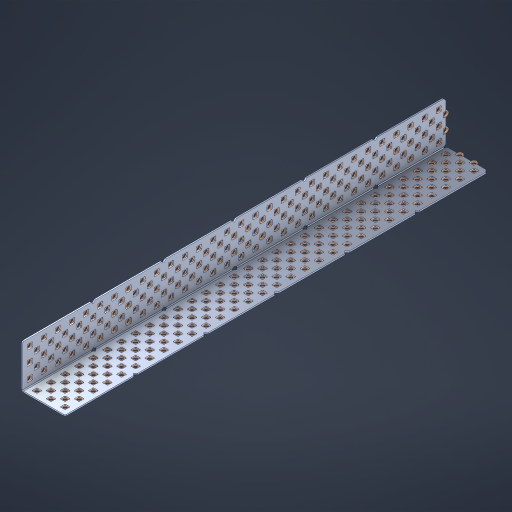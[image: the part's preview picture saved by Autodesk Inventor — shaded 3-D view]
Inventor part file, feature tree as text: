
AUTODESK INVENTOR PART (.ipt)
format: ipt  version: 2023 (Build 270158000, 158)  size: 3,007,488 bytes
history: native  units: in
note: dims shown in document units (in); Inventor stores cm internally (conversion verified against a paired STEP export)
features: other x306, extrude x298, sheet_metal_op x8, sketch x7, pattern_linear x3, mirror x1, chamfer x1
ambient origin geometry x8: Origin, YZ Plane, XZ Plane, XY Plane, X Axis, Y Axis, Z Axis, Center Point
bodies: Solid1 (feature_tree), Body (feature_tree)
feature tree (624):
  sheet_metal_op  "Flanges"
  sheet_metal_op  "Body Pattern"
  pattern_linear  "Center Double"  Spacing1=1.5in  [1 undecoded]
  pattern_linear  "Center Pattern"  Spacing1=0.1875in  [1 undecoded]
  other  "Arc Length"
  pattern_linear  "Notch Pattern"  Spacing1=0.0469in  [1 undecoded]
  other  "Diagonal Plane"
  mirror  "Everything Mirrored"
  chamfer  "End Chamfer"
  sketch  "Sketch1"  dims[d0=1.5in]
  other  "Plate1"
  sketch  "Sketch2"  dims[d1=15.0in]
  other  "Plate2"
  sheet_metal_op  "Bend1"
  sheet_metal_op  "Corner1"
  sketch  "Sketch8"  dims[d2=0.0469in]
  sketch  "Sketch9"  dims[d3=0.0469in]
  other  "Srf91"
  sheet_metal_op  "Body Pattern Sketch"
  other  "Srf92"
  sketch  "Sketch13"  dims[d4=0.0234in]
  sketch  "Sketch15"  dims[d5=0.0938in]
  sketch  "Sketch16"  dims[d6=0.0469in d7=1.5in d8=90.0deg d9=0.0312in d10=0.1875in d11=0.0469in d12=0.0469in d49=0.182in d50=0.02in d52=0.25in d53=0.0469in d54=0.0in d55=0.172in d56=1.0in d57=0.0in d85=0.1473in d86=0.1659in d89=0.0469in d90=0.0in d91=0.04in d92=0.0491in d95=2.5in d96=0.04in d97=0.25in d98=45.0deg d106=0.182in d107=0.02in d110=0.0469in d111=0.0in d112=0.172in d113=0.5in d114=0.0in d117=0.5in d126=0.0491in d127=0.1227in d128=0.08in d129=0.04in d130=2.5in d131=0.25in d132=11.811in d134=0.5in d135=1.1811in d137=0.5in d140=0.5in d141=1.0in d142=0.3937in d144=0.5in d145=0.071in d146=0.7874in d148=0.5in]
  other  "Srf786"
  other  "Srf856"
  other  "Srf889"
  other  "Srf890"
  other  "Srf891"
  other  "Srf1275"
  other  "Srf1276"
  other  "Srf1278"
  other  "Srf1277"
  other  "Srf1285"
  other  "Srf1286"
  other  "Srf1287"
  other  "Srf1445"
  other  "Srf1446"
  other  "Srf1447"
  other  "Srf1448"
  other  "Srf1449"
  other  "Srf1537"
  other  "Srf1538"
  other  "Srf1539"
  other  "Srf1540"
  other  "Srf1541"
  other  "Srf1807"
  other  "Srf1808"
  other  "Srf1809"
  other  "Srf1810"
  other  "Srf1811"
  other  "Srf1812"
  other  "Srf1813"
  other  "Srf1814"
  other  "Srf1815"
  other  "Srf1816"
  other  "Srf1817"
  other  "Srf1818"
  other  "Srf1819"
  other  "Srf1820"
  other  "Srf1821"
  other  "Srf1822"
  other  "Srf1823"
  other  "Srf1824"
  other  "Srf1825"
  other  "Srf1826"
  other  "Srf1827"
  other  "Srf1959"
  other  "Srf1960"
  other  "Srf1961"
  other  "Srf1962"
  other  "Srf1963"
  other  "Srf1964"
  other  "Srf1965"
  other  "Srf1966"
  other  "Srf1967"
  other  "Srf1968"
  other  "Srf1969"
  other  "Srf1970"
  other  "Srf1971"
  other  "Srf1972"
  other  "Srf1973"
  other  "Srf1974"
  other  "Srf1975"
  other  "Srf1976"
  other  "Srf1977"
  other  "Srf1978"
  other  "Srf1979"
  other  "Srf2009"
  other  "Srf2010"
  other  "Srf2011"
  other  "Srf2012"
  other  "Srf2013"
  other  "Srf2014"
  other  "Srf2015"
  other  "Srf2016"
  other  "Srf2017"
  other  "Srf2018"
  other  "Srf2019"
  other  "Srf2020"
  other  "Srf2021"
  other  "Srf2022"
  other  "Srf2023"
  other  "Srf2024"
  other  "Srf2025"
  other  "Srf2026"
  other  "Srf2027"
  other  "Srf2028"
  other  "Srf2029"
  other  "Srf2030"
  other  "Srf2031"
  other  "Srf2032"
  other  "Srf2033"
  other  "Srf2034"
  other  "Srf2035"
  other  "Srf2036"
  other  "Srf2037"
  other  "Srf2038"
  other  "Srf2043"
  other  "Srf2044"
  other  "Srf2045"
  other  "Srf2046"
  other  "Srf2047"
  other  "Srf2048"
  other  "Srf2049"
  other  "Srf2050"
  other  "Srf2051"
  other  "Srf2052"
  other  "Srf2053"
  other  "Srf2054"
  other  "Srf2055"
  other  "Srf2056"
  other  "Srf2057"
  other  "Srf2058"
  other  "Srf2059"
  other  "Srf2060"
  other  "Srf2061"
  other  "Srf2062"
  other  "Srf2063"
  other  "Srf2064"
  other  "Srf2065"
  other  "Srf2066"
  other  "Srf2067"
  other  "Srf2068"
  other  "Srf2069"
  other  "Srf2070"
  other  "Srf2071"
  other  "Srf2076"
  other  "Srf2077"
  other  "Srf2078"
  other  "Srf2079"
  other  "Srf2080"
  other  "Srf2081"
  other  "Srf2082"
  other  "Srf2083"
  other  "Srf2084"
  other  "Srf2085"
  other  "Srf2086"
  other  "Srf2087"
  other  "Srf2088"
  other  "Srf2089"
  other  "Srf2090"
  other  "Srf2091"
  other  "Srf2092"
  other  "Srf2093"
  other  "Srf2094"
  other  "Srf2095"
  other  "Srf2096"
  other  "Srf2097"
  other  "Srf2098"
  other  "Srf2099"
  other  "Srf2100"
  other  "Srf2101"
  other  "Srf2102"
  other  "Srf2103"
  other  "Srf2104"
  other  "Srf2105"
  other  "Srf2106"
  other  "Srf2107"
  other  "Srf2108"
  other  "Srf2109"
  other  "Srf2110"
  other  "Srf2111"
  other  "Srf2112"
  other  "Srf2113"
  other  "Srf2114"
  other  "Srf2115"
  other  "Srf2116"
  other  "Srf2117"
  other  "Srf2118"
  other  "Srf2119"
  other  "Srf2120"
  other  "Srf2121"
  other  "Srf2122"
  other  "Srf2123"
  other  "Srf2124"
  other  "Srf2125"
  other  "Srf2126"
  other  "Srf2127"
  other  "Srf2128"
  other  "Srf2129"
  other  "Srf2130"
  other  "Srf2131"
  other  "Srf2132"
  other  "Srf2133"
  other  "Srf2134"
  other  "Srf2135"
  other  "Srf2136"
  other  "Srf2137"
  other  "Srf2138"
  other  "Srf2139"
  other  "Srf2140"
  other  "Srf2141"
  other  "Srf2142"
  other  "Srf2143"
  other  "Srf2144"
  other  "Srf2145"
  other  "Srf2146"
  other  "Srf2147"
  other  "Srf2148"
  other  "Srf2149"
  other  "Srf2150"
  other  "Srf2151"
  other  "Srf2152"
  other  "Srf2153"
  other  "Srf2154"
  other  "Srf2155"
  other  "Srf2156"
  other  "Srf2157"
  other  "Srf2158"
  other  "Srf2159"
  other  "Srf2160"
  other  "Srf2161"
  other  "Srf2162"
  other  "Srf2163"
  other  "Srf2179"
  other  "Srf2180"
  other  "Srf2181"
  other  "Srf2182"
  other  "Srf2183"
  other  "Srf2184"
  other  "Srf2185"
  other  "Srf2186"
  other  "Srf2187"
  other  "Srf2188"
  other  "Srf2189"
  other  "Srf2190"
  other  "Srf2191"
  other  "Srf2192"
  other  "Srf2193"
  other  "Srf2194"
  other  "Srf2195"
  other  "Srf2196"
  other  "Srf2197"
  other  "Srf2198"
  other  "Srf2199"
  other  "Srf2200"
  other  "Srf2201"
  other  "Srf2202"
  other  "Srf2203"
  other  "Srf2204"
  other  "Srf2205"
  other  "Srf2206"
  other  "Srf2207"
  other  "Srf2208"
  other  "Srf2209"
  other  "Srf2210"
  other  "Srf2211"
  other  "Srf2212"
  other  "Srf2213"
  other  "Srf2214"
  other  "Srf2215"
  other  "Srf2216"
  other  "Srf2217"
  other  "Srf2218"
  other  "Srf2219"
  other  "Srf2220"
  other  "Srf2221"
  other  "Srf2222"
  other  "Srf2223"
  other  "Srf2224"
  other  "Srf2225"
  other  "Srf2226"
  other  "Srf2227"
  other  "Srf2228"
  other  "Srf2229"
  other  "Srf2230"
  other  "Srf2231"
  other  "Srf2232"
  other  "Srf2233"
  other  "Srf2234"
  other  "Srf2235"
  other  "Srf2236"
  other  "Srf2237"
  other  "Srf2238"
  other  "Srf2239"
  other  "Srf2240"
  other  "Srf2241"
  other  "Srf2242"
  other  "Srf2243"
  other  "Srf2244"
  other  "Srf2245"
  other  "Srf2246"
  other  "Srf2247"
  other  "Srf2248"
  other  "Srf2249"
  other  "Srf2250"
  other  "Srf2251"
  other  "Srf2252"
  other  "Srf2253"
  other  "Srf2254"
  other  "Srf2255"
  other  "Srf2256"
  other  "Srf2257"
  other  "Srf2258"
  other  "Srf2259"
  other  "Srf2260"
  other  "Srf2261"
  other  "Srf2262"
  other  "Srf2263"
  other  "Srf2264"
  other  "Srf2265"
  sheet_metal_op  "Body Stamp"
  sheet_metal_op  "Body Circle"
  other  "Center Stamp"
  other  "Center Circle"
  sheet_metal_op  "Notch"
  extrude  "ExtrusionSrf92"  Depth=0.0469in
  extrude  "ExtrusionSrf856"  Depth=0.3937in
  extrude  "ExtrusionSrf889"  Depth=0.02in
  extrude  "ExtrusionSrf890"  Depth=0.25in
  extrude  "ExtrusionSrf891"  Depth=0.0469in
  extrude  "ExtrusionSrf1275"  TaperAngle=0.0deg  [1 undecoded]
  extrude  "ExtrusionSrf1276"  Depth=0.3937in
  extrude  "ExtrusionSrf1277"  Depth=0.3937in TaperAngle=0.0deg
  extrude  "ExtrusionSrf1345"  Depth=0.3937in
  extrude  "ExtrusionSrf1346"  Depth=0.3937in
  extrude  "ExtrusionSrf1347"  Depth=0.0469in
  extrude  "ExtrusionSrf1348"  Depth=0.3937in TaperAngle=0.0deg
  extrude  "ExtrusionSrf1445"  Depth=0.3937in
  extrude  "ExtrusionSrf1446"  Depth=0.25in TaperAngle=45.0deg
  extrude  "ExtrusionSrf1447"  Depth=0.3937in
  extrude  "ExtrusionSrf1448"  Depth=0.02in
  extrude  "ExtrusionSrf1449"  Depth=0.0469in
  extrude  "ExtrusionSrf1537"  TaperAngle=0.0deg  [1 undecoded]
  extrude  "ExtrusionSrf1538"  Depth=0.3937in
  extrude  "ExtrusionSrf1539"  Depth=0.3937in TaperAngle=0.0deg
  extrude  "ExtrusionSrf1540"  Depth=0.3937in
  extrude  "ExtrusionSrf1541"  Depth=0.3937in
  extrude  "ExtrusionSrf1807"  Depth=0.3937in
  extrude  "ExtrusionSrf1808"  Depth=0.3937in
  extrude  "ExtrusionSrf1809"  Depth=0.3937in
  extrude  "ExtrusionSrf1810"  Depth=0.3937in
  extrude  "ExtrusionSrf1811"  Depth=0.25in
  extrude  "ExtrusionSrf1812"  Depth=0.3937in
  extrude  "ExtrusionSrf1813"  Depth=0.3937in
  extrude  "ExtrusionSrf1814"  Depth=0.3937in
  extrude  "ExtrusionSrf1815"  Depth=0.3937in
  extrude  "ExtrusionSrf1816"  Depth=0.3937in
  extrude  "ExtrusionSrf1817"  Depth=0.3937in
  extrude  "ExtrusionSrf1818"  Depth=0.3937in
  extrude  "ExtrusionSrf1819"  [1 undecoded]
  extrude  "ExtrusionSrf1820"  [1 undecoded]
  extrude  "ExtrusionSrf1821"  [1 undecoded]
  extrude  "ExtrusionSrf1822"  [1 undecoded]
  extrude  "ExtrusionSrf1823"  [1 undecoded]
  extrude  "ExtrusionSrf1824"  [1 undecoded]
  extrude  "ExtrusionSrf1825"  [1 undecoded]
  extrude  "ExtrusionSrf1826"  [1 undecoded]
  extrude  "ExtrusionSrf1827"  [1 undecoded]
  extrude  "ExtrusionSrf1959"  [1 undecoded]
  extrude  "ExtrusionSrf1960"  [1 undecoded]
  extrude  "ExtrusionSrf1961"  [1 undecoded]
  extrude  "ExtrusionSrf1962"  [1 undecoded]
  extrude  "ExtrusionSrf1963"  [1 undecoded]
  extrude  "ExtrusionSrf1964"  [1 undecoded]
  extrude  "ExtrusionSrf1965"  [1 undecoded]
  extrude  "ExtrusionSrf1966"  [1 undecoded]
  extrude  "ExtrusionSrf1967"  [1 undecoded]
  extrude  "ExtrusionSrf1968"  [1 undecoded]
  extrude  "ExtrusionSrf1969"  [1 undecoded]
  extrude  "ExtrusionSrf1970"  [1 undecoded]
  extrude  "ExtrusionSrf1971"  [1 undecoded]
  extrude  "ExtrusionSrf1972"  [1 undecoded]
  extrude  "ExtrusionSrf1973"  [1 undecoded]
  extrude  "ExtrusionSrf1974"  [1 undecoded]
  extrude  "ExtrusionSrf1975"  [1 undecoded]
  extrude  "ExtrusionSrf1976"  [1 undecoded]
  extrude  "ExtrusionSrf1977"  [1 undecoded]
  extrude  "ExtrusionSrf1978"  [1 undecoded]
  extrude  "ExtrusionSrf1979"  [1 undecoded]
  extrude  "ExtrusionSrf2009"  [1 undecoded]
  extrude  "ExtrusionSrf2010"  [1 undecoded]
  extrude  "ExtrusionSrf2011"  [1 undecoded]
  extrude  "ExtrusionSrf2012"  [1 undecoded]
  extrude  "ExtrusionSrf2013"  [1 undecoded]
  extrude  "ExtrusionSrf2014"  [1 undecoded]
  extrude  "ExtrusionSrf2015"  [1 undecoded]
  extrude  "ExtrusionSrf2016"  [1 undecoded]
  extrude  "ExtrusionSrf2017"  [1 undecoded]
  extrude  "ExtrusionSrf2018"  [1 undecoded]
  extrude  "ExtrusionSrf2019"  [1 undecoded]
  extrude  "ExtrusionSrf2020"  [1 undecoded]
  extrude  "ExtrusionSrf2021"  [1 undecoded]
  extrude  "ExtrusionSrf2022"  [1 undecoded]
  extrude  "ExtrusionSrf2023"  [1 undecoded]
  extrude  "ExtrusionSrf2024"  [1 undecoded]
  extrude  "ExtrusionSrf2025"  [1 undecoded]
  extrude  "ExtrusionSrf2026"  [1 undecoded]
  extrude  "ExtrusionSrf2027"  [1 undecoded]
  extrude  "ExtrusionSrf2028"  [1 undecoded]
  extrude  "ExtrusionSrf2029"  [1 undecoded]
  extrude  "ExtrusionSrf2030"  [1 undecoded]
  extrude  "ExtrusionSrf2031"  [1 undecoded]
  extrude  "ExtrusionSrf2032"  [1 undecoded]
  extrude  "ExtrusionSrf2033"  [1 undecoded]
  extrude  "ExtrusionSrf2034"  [1 undecoded]
  extrude  "ExtrusionSrf2035"  [1 undecoded]
  extrude  "ExtrusionSrf2036"  [1 undecoded]
  extrude  "ExtrusionSrf2037"  [1 undecoded]
  extrude  "ExtrusionSrf2038"  [1 undecoded]
  extrude  "ExtrusionSrf2043"  [1 undecoded]
  extrude  "ExtrusionSrf2044"  [1 undecoded]
  extrude  "ExtrusionSrf2045"  [1 undecoded]
  extrude  "ExtrusionSrf2046"  [1 undecoded]
  extrude  "ExtrusionSrf2047"  [1 undecoded]
  extrude  "ExtrusionSrf2048"  [1 undecoded]
  extrude  "ExtrusionSrf2049"  [1 undecoded]
  extrude  "ExtrusionSrf2050"  [1 undecoded]
  extrude  "ExtrusionSrf2051"  [1 undecoded]
  extrude  "ExtrusionSrf2052"  [1 undecoded]
  extrude  "ExtrusionSrf2053"  [1 undecoded]
  extrude  "ExtrusionSrf2054"  [1 undecoded]
  extrude  "ExtrusionSrf2055"  [1 undecoded]
  extrude  "ExtrusionSrf2056"  [1 undecoded]
  extrude  "ExtrusionSrf2057"  [1 undecoded]
  extrude  "ExtrusionSrf2058"  [1 undecoded]
  extrude  "ExtrusionSrf2059"  [1 undecoded]
  extrude  "ExtrusionSrf2060"  [1 undecoded]
  extrude  "ExtrusionSrf2061"  [1 undecoded]
  extrude  "ExtrusionSrf2062"  [1 undecoded]
  extrude  "ExtrusionSrf2063"  [1 undecoded]
  extrude  "ExtrusionSrf2064"  [1 undecoded]
  extrude  "ExtrusionSrf2065"  [1 undecoded]
  extrude  "ExtrusionSrf2066"  [1 undecoded]
  extrude  "ExtrusionSrf2067"  [1 undecoded]
  extrude  "ExtrusionSrf2068"  [1 undecoded]
  extrude  "ExtrusionSrf2069"  [1 undecoded]
  extrude  "ExtrusionSrf2070"  [1 undecoded]
  extrude  "ExtrusionSrf2071"  [1 undecoded]
  extrude  "ExtrusionSrf2076"  [1 undecoded]
  extrude  "ExtrusionSrf2077"  [1 undecoded]
  extrude  "ExtrusionSrf2078"  [1 undecoded]
  extrude  "ExtrusionSrf2079"  [1 undecoded]
  extrude  "ExtrusionSrf2080"  [1 undecoded]
  extrude  "ExtrusionSrf2081"  [1 undecoded]
  extrude  "ExtrusionSrf2082"  [1 undecoded]
  extrude  "ExtrusionSrf2083"  [1 undecoded]
  extrude  "ExtrusionSrf2084"  [1 undecoded]
  extrude  "ExtrusionSrf2085"  [1 undecoded]
  extrude  "ExtrusionSrf2086"  [1 undecoded]
  extrude  "ExtrusionSrf2087"  [1 undecoded]
  extrude  "ExtrusionSrf2088"  [1 undecoded]
  extrude  "ExtrusionSrf2089"  [1 undecoded]
  extrude  "ExtrusionSrf2090"  [1 undecoded]
  extrude  "ExtrusionSrf2091"  [1 undecoded]
  extrude  "ExtrusionSrf2092"  [1 undecoded]
  extrude  "ExtrusionSrf2093"  [1 undecoded]
  extrude  "ExtrusionSrf2094"  [1 undecoded]
  extrude  "ExtrusionSrf2095"  [1 undecoded]
  extrude  "ExtrusionSrf2096"  [1 undecoded]
  extrude  "ExtrusionSrf2097"  [1 undecoded]
  extrude  "ExtrusionSrf2098"  [1 undecoded]
  extrude  "ExtrusionSrf2099"  [1 undecoded]
  extrude  "ExtrusionSrf2100"  [1 undecoded]
  extrude  "ExtrusionSrf2101"  [1 undecoded]
  extrude  "ExtrusionSrf2102"  [1 undecoded]
  extrude  "ExtrusionSrf2103"  [1 undecoded]
  extrude  "ExtrusionSrf2104"  [1 undecoded]
  extrude  "ExtrusionSrf2105"  [1 undecoded]
  extrude  "ExtrusionSrf2106"  [1 undecoded]
  extrude  "ExtrusionSrf2107"  [1 undecoded]
  extrude  "ExtrusionSrf2108"  [1 undecoded]
  extrude  "ExtrusionSrf2109"  [1 undecoded]
  extrude  "ExtrusionSrf2110"  [1 undecoded]
  extrude  "ExtrusionSrf2111"  [1 undecoded]
  extrude  "ExtrusionSrf2112"  [1 undecoded]
  extrude  "ExtrusionSrf2113"  [1 undecoded]
  extrude  "ExtrusionSrf2114"  [1 undecoded]
  extrude  "ExtrusionSrf2115"  [1 undecoded]
  extrude  "ExtrusionSrf2116"  [1 undecoded]
  extrude  "ExtrusionSrf2117"  [1 undecoded]
  extrude  "ExtrusionSrf2118"  [1 undecoded]
  extrude  "ExtrusionSrf2119"  [1 undecoded]
  extrude  "ExtrusionSrf2120"  [1 undecoded]
  extrude  "ExtrusionSrf2121"  [1 undecoded]
  extrude  "ExtrusionSrf2122"  [1 undecoded]
  extrude  "ExtrusionSrf2123"  [1 undecoded]
  extrude  "ExtrusionSrf2124"  [1 undecoded]
  extrude  "ExtrusionSrf2125"  [1 undecoded]
  extrude  "ExtrusionSrf2126"  [1 undecoded]
  extrude  "ExtrusionSrf2127"  [1 undecoded]
  extrude  "ExtrusionSrf2128"  [1 undecoded]
  extrude  "ExtrusionSrf2129"  [1 undecoded]
  extrude  "ExtrusionSrf2130"  [1 undecoded]
  extrude  "ExtrusionSrf2131"  [1 undecoded]
  extrude  "ExtrusionSrf2132"  [1 undecoded]
  extrude  "ExtrusionSrf2133"  [1 undecoded]
  extrude  "ExtrusionSrf2134"  [1 undecoded]
  extrude  "ExtrusionSrf2135"  [1 undecoded]
  extrude  "ExtrusionSrf2136"  [1 undecoded]
  extrude  "ExtrusionSrf2137"  [1 undecoded]
  extrude  "ExtrusionSrf2138"  [1 undecoded]
  extrude  "ExtrusionSrf2139"  [1 undecoded]
  extrude  "ExtrusionSrf2140"  [1 undecoded]
  extrude  "ExtrusionSrf2141"  [1 undecoded]
  extrude  "ExtrusionSrf2142"  [1 undecoded]
  extrude  "ExtrusionSrf2143"  [1 undecoded]
  extrude  "ExtrusionSrf2144"  [1 undecoded]
  extrude  "ExtrusionSrf2145"  [1 undecoded]
  extrude  "ExtrusionSrf2146"  [1 undecoded]
  extrude  "ExtrusionSrf2147"  [1 undecoded]
  extrude  "ExtrusionSrf2148"  [1 undecoded]
  extrude  "ExtrusionSrf2149"  [1 undecoded]
  extrude  "ExtrusionSrf2150"  [1 undecoded]
  extrude  "ExtrusionSrf2151"  [1 undecoded]
  extrude  "ExtrusionSrf2152"  [1 undecoded]
  extrude  "ExtrusionSrf2153"  [1 undecoded]
  extrude  "ExtrusionSrf2154"  [1 undecoded]
  extrude  "ExtrusionSrf2155"  [1 undecoded]
  extrude  "ExtrusionSrf2156"  [1 undecoded]
  extrude  "ExtrusionSrf2157"  [1 undecoded]
  extrude  "ExtrusionSrf2158"  [1 undecoded]
  extrude  "ExtrusionSrf2159"  [1 undecoded]
  extrude  "ExtrusionSrf2160"  [1 undecoded]
  extrude  "ExtrusionSrf2161"  [1 undecoded]
  extrude  "ExtrusionSrf2162"  [1 undecoded]
  extrude  "ExtrusionSrf2163"  [1 undecoded]
  extrude  "ExtrusionSrf2179"  [1 undecoded]
  extrude  "ExtrusionSrf2180"  [1 undecoded]
  extrude  "ExtrusionSrf2181"  [1 undecoded]
  extrude  "ExtrusionSrf2182"  [1 undecoded]
  extrude  "ExtrusionSrf2183"  [1 undecoded]
  extrude  "ExtrusionSrf2184"  [1 undecoded]
  extrude  "ExtrusionSrf2185"  [1 undecoded]
  extrude  "ExtrusionSrf2186"  [1 undecoded]
  extrude  "ExtrusionSrf2187"  [1 undecoded]
  extrude  "ExtrusionSrf2188"  [1 undecoded]
  extrude  "ExtrusionSrf2189"  [1 undecoded]
  extrude  "ExtrusionSrf2190"  [1 undecoded]
  extrude  "ExtrusionSrf2191"  [1 undecoded]
  extrude  "ExtrusionSrf2192"  [1 undecoded]
  extrude  "ExtrusionSrf2193"  [1 undecoded]
  extrude  "ExtrusionSrf2194"  [1 undecoded]
  extrude  "ExtrusionSrf2195"  [1 undecoded]
  extrude  "ExtrusionSrf2196"  [1 undecoded]
  extrude  "ExtrusionSrf2197"  [1 undecoded]
  extrude  "ExtrusionSrf2198"  [1 undecoded]
  extrude  "ExtrusionSrf2199"  [1 undecoded]
  extrude  "ExtrusionSrf2200"  [1 undecoded]
  extrude  "ExtrusionSrf2201"  [1 undecoded]
  extrude  "ExtrusionSrf2202"  [1 undecoded]
  extrude  "ExtrusionSrf2203"  [1 undecoded]
  extrude  "ExtrusionSrf2204"  [1 undecoded]
  extrude  "ExtrusionSrf2205"  [1 undecoded]
  extrude  "ExtrusionSrf2206"  [1 undecoded]
  extrude  "ExtrusionSrf2207"  [1 undecoded]
  extrude  "ExtrusionSrf2208"  [1 undecoded]
  extrude  "ExtrusionSrf2209"  [1 undecoded]
  extrude  "ExtrusionSrf2210"  [1 undecoded]
  extrude  "ExtrusionSrf2211"  [1 undecoded]
  extrude  "ExtrusionSrf2212"  [1 undecoded]
  extrude  "ExtrusionSrf2213"  [1 undecoded]
  extrude  "ExtrusionSrf2214"  [1 undecoded]
  extrude  "ExtrusionSrf2215"  [1 undecoded]
  extrude  "ExtrusionSrf2216"  [1 undecoded]
  extrude  "ExtrusionSrf2217"  [1 undecoded]
  extrude  "ExtrusionSrf2218"  [1 undecoded]
  extrude  "ExtrusionSrf2219"  [1 undecoded]
  extrude  "ExtrusionSrf2220"  [1 undecoded]
  extrude  "ExtrusionSrf2221"  [1 undecoded]
  extrude  "ExtrusionSrf2222"  [1 undecoded]
  extrude  "ExtrusionSrf2223"  [1 undecoded]
  extrude  "ExtrusionSrf2224"  [1 undecoded]
  extrude  "ExtrusionSrf2225"  [1 undecoded]
  extrude  "ExtrusionSrf2226"  [1 undecoded]
  extrude  "ExtrusionSrf2227"  [1 undecoded]
  extrude  "ExtrusionSrf2228"  [1 undecoded]
  extrude  "ExtrusionSrf2229"  [1 undecoded]
  extrude  "ExtrusionSrf2230"  [1 undecoded]
  extrude  "ExtrusionSrf2231"  [1 undecoded]
  extrude  "ExtrusionSrf2232"  [1 undecoded]
  extrude  "ExtrusionSrf2233"  [1 undecoded]
  extrude  "ExtrusionSrf2234"  [1 undecoded]
  extrude  "ExtrusionSrf2235"  [1 undecoded]
  extrude  "ExtrusionSrf2236"  [1 undecoded]
  extrude  "ExtrusionSrf2237"  [1 undecoded]
  extrude  "ExtrusionSrf2238"  [1 undecoded]
  extrude  "ExtrusionSrf2239"  [1 undecoded]
  extrude  "ExtrusionSrf2240"  [1 undecoded]
  extrude  "ExtrusionSrf2241"  [1 undecoded]
  extrude  "ExtrusionSrf2242"  [1 undecoded]
  extrude  "ExtrusionSrf2243"  [1 undecoded]
  extrude  "ExtrusionSrf2244"  [1 undecoded]
  extrude  "ExtrusionSrf2245"  [1 undecoded]
  extrude  "ExtrusionSrf2246"  [1 undecoded]
  extrude  "ExtrusionSrf2247"  [1 undecoded]
  extrude  "ExtrusionSrf2248"  [1 undecoded]
  extrude  "ExtrusionSrf2249"  [1 undecoded]
  extrude  "ExtrusionSrf2250"  [1 undecoded]
  extrude  "ExtrusionSrf2251"  [1 undecoded]
  extrude  "ExtrusionSrf2252"  [1 undecoded]
  extrude  "ExtrusionSrf2253"  [1 undecoded]
  extrude  "ExtrusionSrf2254"  [1 undecoded]
  extrude  "ExtrusionSrf2255"  [1 undecoded]
  extrude  "ExtrusionSrf2256"  [1 undecoded]
  extrude  "ExtrusionSrf2257"  [1 undecoded]
  extrude  "ExtrusionSrf2258"  [1 undecoded]
  extrude  "ExtrusionSrf2259"  [1 undecoded]
  extrude  "ExtrusionSrf2260"  [1 undecoded]
  extrude  "ExtrusionSrf2261"  [1 undecoded]
  extrude  "ExtrusionSrf2262"  [1 undecoded]
  extrude  "ExtrusionSrf2263"  [1 undecoded]
  extrude  "ExtrusionSrf2264"  [1 undecoded]
  extrude  "ExtrusionSrf2265"  [1 undecoded]
note: 269 required parameter values undecoded (feature->parameter linkage not recoverable at this tier; creation-order binding heuristic only, values carry confidence <= 0.55)
